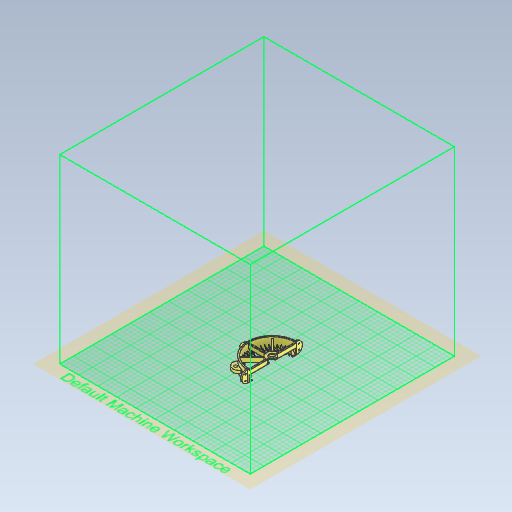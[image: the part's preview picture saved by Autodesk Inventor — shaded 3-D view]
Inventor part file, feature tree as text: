
AUTODESK INVENTOR PART (.ipt)
format: ipt  version: 2021.3 (Build 253353010, 353A)  size: 1,406,464 bytes
history: native  units: in
note: dims shown in document units (in); Inventor stores cm internally (conversion verified against a paired STEP export)
features: extrude x12, sketch x12, plane x4, pattern_circular x3, fillet x2
ambient origin geometry x8: Origin, YZ Plane, XZ Plane, XY Plane, X Axis, Y Axis, Z Axis, Center Point
bodies: Solid1 (feature_tree)
feature tree (33):
  extrude  "Extrusion1"  Depth=4.25in
  plane  "Work Plane1"
  plane  "Work Plane2"
  extrude  "Extrusion3"  Depth=1.0in
  fillet  "Fillet1"  Radius=2.125in
  extrude  "Extrusion4"  TaperAngle=0.0deg  [1 undecoded]
  pattern_circular  "Circular Pattern2"  Count=2 Angle=360.0deg
  plane  "Work Plane3"
  extrude  "Extrusion5"  Depth=1.0in
  extrude  "Extrusion6"  Depth=0.5in
  fillet  "Fillet2"  [1 undecoded]
  extrude  "Extrusion7"  Depth=0.5in TaperAngle=0.0deg
  pattern_circular  "Circular Pattern3"  [2 undecoded]
  extrude  "Extrusion14"  Depth=0.3543in
  pattern_circular  "Circular Pattern9"  [2 undecoded]
  extrude  "Extrusion15"  Depth=0.3543in TaperAngle=360.0deg
  plane  "Work Plane4"
  extrude  "Extrusion16"  Depth=0.3543in
  extrude  "Extrusion17"  Depth=0.125in
  extrude  "Extrusion18"  Depth=0.3543in
  extrude  "Extrusion19"  Depth=0.3543in
  sketch  "Sketch1"  dims[d0=4.0in d1=4.25in]
  sketch  "Sketch3"  dims[d2=1.0in d3=0.0in d4=1.4in d10=2.125in]
  sketch  "Sketch4"  dims[d11=0.25in d12=0.0in]
  sketch  "Sketch5"  dims[d13=0.5in d14=0.0in]
  sketch  "Sketch6"  dims[d15=0.5in]
  sketch  "Sketch7"  dims[d16=0.125in]
  sketch  "Sketch8"  dims[d17=0.2in]
  sketch  "Sketch11"  dims[d18=0.5in d19=0.0in d20=0.7874in d21=360.0deg]
  sketch  "Sketch12"  dims[d23=-2.125in d24=1.0in]
  sketch  "Sketch13"  dims[d25=0.25in d26=0.5in d27=0.0in]
  sketch  "Sketch14"  dims[d28=0.1in d29=0.0in d30=0.5in d31=0.0in]
  sketch  "Sketch15"  dims[d32=0.5in d33=0.25in d34=0.2in d35=0.5in d36=0.0in d37=2.3622in d38=360.0deg d40=0.25in d41=0.125in d42=0.25in d43=0.2in d49=0.5in d50=0.0312in d79=0.65in d80=0.0in d81=18.8976in d82=360.0deg d84=3.4625in d85=0.0in d86=0.0777in d87=-0.4688in d88=4.0in d89=90.0deg d90=0.25in d91=4.0in d92=0.0in d93=0.125in d94=4.0in d95=45.0deg d96=0.125in d97=4.0in d98=135.0deg d99=0.125in d100=1.0236in d101=0.8661in d102=0.3543in d103=0.0in d104=0.5512in d105=0.0787in d106=0.0in d107=0.0787in d108=0.0in d109=0.0in d110=0.0in]
note: 6 required parameter values undecoded (feature->parameter linkage not recoverable at this tier; creation-order binding heuristic only, values carry confidence <= 0.55)
